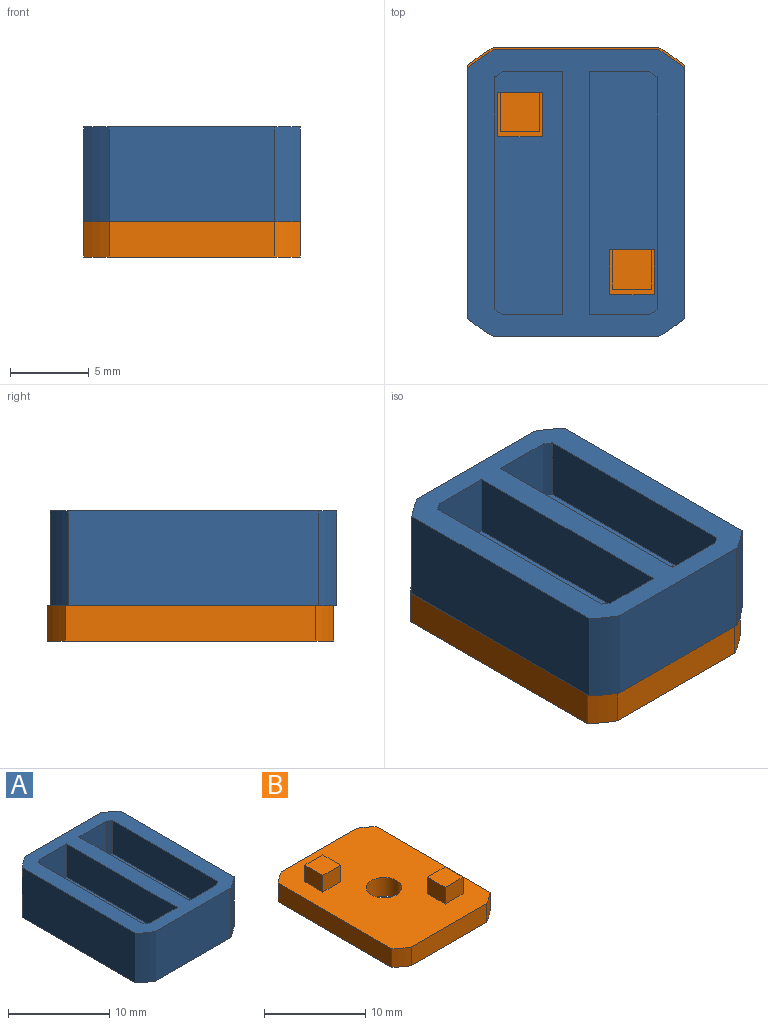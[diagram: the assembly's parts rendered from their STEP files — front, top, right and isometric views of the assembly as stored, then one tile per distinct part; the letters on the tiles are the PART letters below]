
ASSEMBLY  parts=2 mates=1
PART A: 32 faces, bbox 13.7x18.2x6 mm
  f0: plane 18.19x13.72mm, normal (0,0,-1), area 229.8mm2, adj f3,f4,f5,f6,f7,f8,f9,f22
  f1: plane 15.4x4.3mm, normal (0,0,1), area 57.9mm2, adj f15,f16,f17,f18,f19,f21,f28,f29
  f2: plane 15.4x4.3mm, normal (0,0,1), area 57.9mm2, adj f10,f11,f12,f13,f14,f20,f24,f25
  f3: plane 15.9x6mm, normal (1,0,0), area 95.4mm2, adj f0,f4,f22,f23
  f4: cylinder r=10.5mm len=6mm, axis (0,0,-1), area 11.9mm2, adj f0,f3,f5,f23
  f5: plane 10.5x6mm, normal (0,1,0), area 63mm2, adj f0,f4,f6,f23
  f6: cylinder r=10.5mm len=6mm, axis (0,0,-1), area 11.9mm2, adj f0,f5,f7,f23
  f7: plane 15.9x6mm, normal (-1,0,0), area 95.4mm2, adj f0,f6,f8,f23
  f8: cylinder r=10.5mm len=6mm, axis (0,0,-1), area 11.9mm2, adj f0,f7,f9,f23
  f9: plane 10.5x6mm, normal (0,-1,0), area 63mm2, adj f0,f8,f22,f23
  f10: cylinder r=9mm len=4mm, axis (0,0,-1), area 2.3mm2, adj f2,f11,f20,f23
  f11: plane 4x3.81mm, normal (0,-1,0), area 15.2mm2, adj f2,f10,f12,f23
  f12: plane 15.4x4mm, normal (-1,0,0), area 61.6mm2, adj f2,f11,f13,f23
  f13: plane 4x3.81mm, normal (0,1,0), area 15.2mm2, adj f2,f12,f14,f23
  f14: cylinder r=9mm len=4mm, axis (0,0,-1), area 2.3mm2, adj f2,f13,f20,f23
  f15: plane 4x3.81mm, normal (0,-1,0), area 15.2mm2, adj f1,f16,f21,f23
  f16: cylinder r=9mm len=4mm, axis (0,0,-1), area 2.3mm2, adj f1,f15,f17,f23
  f17: plane 14.76x4mm, normal (-1,0,0), area 59mm2, adj f1,f16,f18,f23
  f18: cylinder r=9mm len=4mm, axis (0,0,-1), area 2.3mm2, adj f1,f17,f19,f23
  f19: plane 4x3.81mm, normal (0,1,0), area 15.2mm2, adj f1,f18,f21,f23
  f20: plane 14.76x4mm, normal (1,0,0), area 59mm2, adj f2,f10,f14,f23
  f21: plane 15.4x4mm, normal (1,0,0), area 61.6mm2, adj f1,f15,f19,f23
  f22: cylinder r=10.5mm len=6mm, axis (0,0,-1), area 11.9mm2, adj f0,f3,f9,f23
  f23: plane 18.19x13.72mm, normal (0,0,1), area 113.9mm2, adj f3,f4,f5,f6,f7,f8,f9,f10
  f24: plane 2.85x2mm, normal (0,-1,0), area 5.7mm2, adj f0,f2,f25,f27
  f25: plane 2.85x2mm, normal (-1,0,0), area 5.7mm2, adj f0,f2,f24,f26
  f26: plane 2.85x2mm, normal (0,1,0), area 5.7mm2, adj f0,f2,f25,f27
  f27: plane 2.85x2mm, normal (1,0,0), area 5.7mm2, adj f0,f2,f24,f26
  f28: plane 2.85x2mm, normal (0,-1,0), area 5.7mm2, adj f0,f1,f29,f31
  f29: plane 2.85x2mm, normal (-1,0,0), area 5.7mm2, adj f0,f1,f28,f30
  f30: plane 2.85x2mm, normal (0,1,0), area 5.7mm2, adj f0,f1,f29,f31
  f31: plane 2.85x2mm, normal (1,0,0), area 5.7mm2, adj f0,f1,f28,f30
PART B: 21 faces, bbox 13.7x18.2x4.3 mm
  f0: plane 18.19x13.72mm, normal (0,0,1), area 223.9mm2, adj f1,f2,f3,f4,f5,f6,f7,f8
  f1: cylinder r=10.5mm len=2.25mm, axis (0,0,-1), area 4.4mm2, adj f0,f2,f8,f9
  f2: plane 15.9x2.25mm, normal (1,0,0), area 35.8mm2, adj f0,f1,f3,f9
  f3: cylinder r=10.5mm len=2.25mm, axis (0,0,-1), area 4.4mm2, adj f0,f2,f4,f9
  f4: plane 10.5x2.25mm, normal (0,1,0), area 23.6mm2, adj f0,f3,f5,f9
  f5: cylinder r=10.5mm len=2.25mm, axis (0,0,-1), area 4.4mm2, adj f0,f4,f6,f9
  f6: plane 15.9x2.25mm, normal (-1,0,0), area 35.8mm2, adj f0,f5,f7,f9
  f7: cylinder r=10.5mm len=2.25mm, axis (0,0,-1), area 4.4mm2, adj f0,f6,f8,f9
  f8: plane 10.5x2.25mm, normal (0,-1,0), area 23.6mm2, adj f0,f1,f7,f9
  f9: plane 18.19x13.72mm, normal (0,0,-1), area 236.4mm2, adj f1,f2,f3,f4,f5,f6,f7,f8
  f10: cylinder r=1.75mm len=3.5mm, axis (0,0,1), area 24.7mm2, adj f0,f9
  f11: plane 2.5x2mm, normal (0,-1,0), area 5mm2, adj f0,f12,f14,f15
  f12: plane 2.5x2mm, normal (1,0,0), area 5mm2, adj f0,f11,f13,f15
  f13: plane 2.5x2mm, normal (0,1,0), area 5mm2, adj f0,f12,f14,f15
  f14: plane 2.5x2mm, normal (-1,0,0), area 5mm2, adj f0,f11,f13,f15
  f15: plane 2.5x2.5mm, normal (0,0,1), area 6.2mm2, adj f11,f12,f13,f14
  f16: plane 2.5x2mm, normal (0,1,0), area 5mm2, adj f0,f17,f19,f20
  f17: plane 2.5x2mm, normal (-1,0,0), area 5mm2, adj f0,f16,f18,f20
  f18: plane 2.5x2mm, normal (0,-1,0), area 5mm2, adj f0,f17,f19,f20
  f19: plane 2.5x2mm, normal (1,0,0), area 5mm2, adj f0,f16,f18,f20
  f20: plane 2.5x2.5mm, normal (0,0,1), area 6.2mm2, adj f16,f17,f18,f19
PLACE A t=(-14.56,7.06,-5.77)mm
PLACE B t=(45.44,7.24,-8.02)mm
MATE fastened B.f15 <-> A.f2  axis (0,0,1) through (11.89,13.49,-3.77)mm
